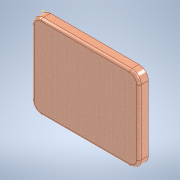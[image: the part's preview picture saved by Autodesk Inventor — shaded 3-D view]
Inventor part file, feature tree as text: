
AUTODESK INVENTOR PART (.ipt)
format: ipt  version: 2021.1 (Build 251245000, 245)  size: 154,624 bytes
history: native  units: in
note: dims shown in document units (in); Inventor stores cm internally (conversion verified against a paired STEP export)
features: sketch x2, extrude x1, fillet x1
ambient origin geometry x8: Origin, YZ Plane, XZ Plane, XY Plane, X Axis, Y Axis, Z Axis, Center Point
bodies: Solid1 (feature_tree)
feature tree (4):
  extrude  "Extrusion1"  Depth=18.0in
  fillet  "Fillet1"  Radius=2.0in
  sketch  "Sketch2"  dims[d3=2.0in d4=2.0in d5=0.0in d6=0.5in d7=1.8in d8=1.1in d9=6.0in d10=4.0in]
  sketch  "Sketch1"  dims[d0=23.0in d1=18.0in d2=2.0in]
